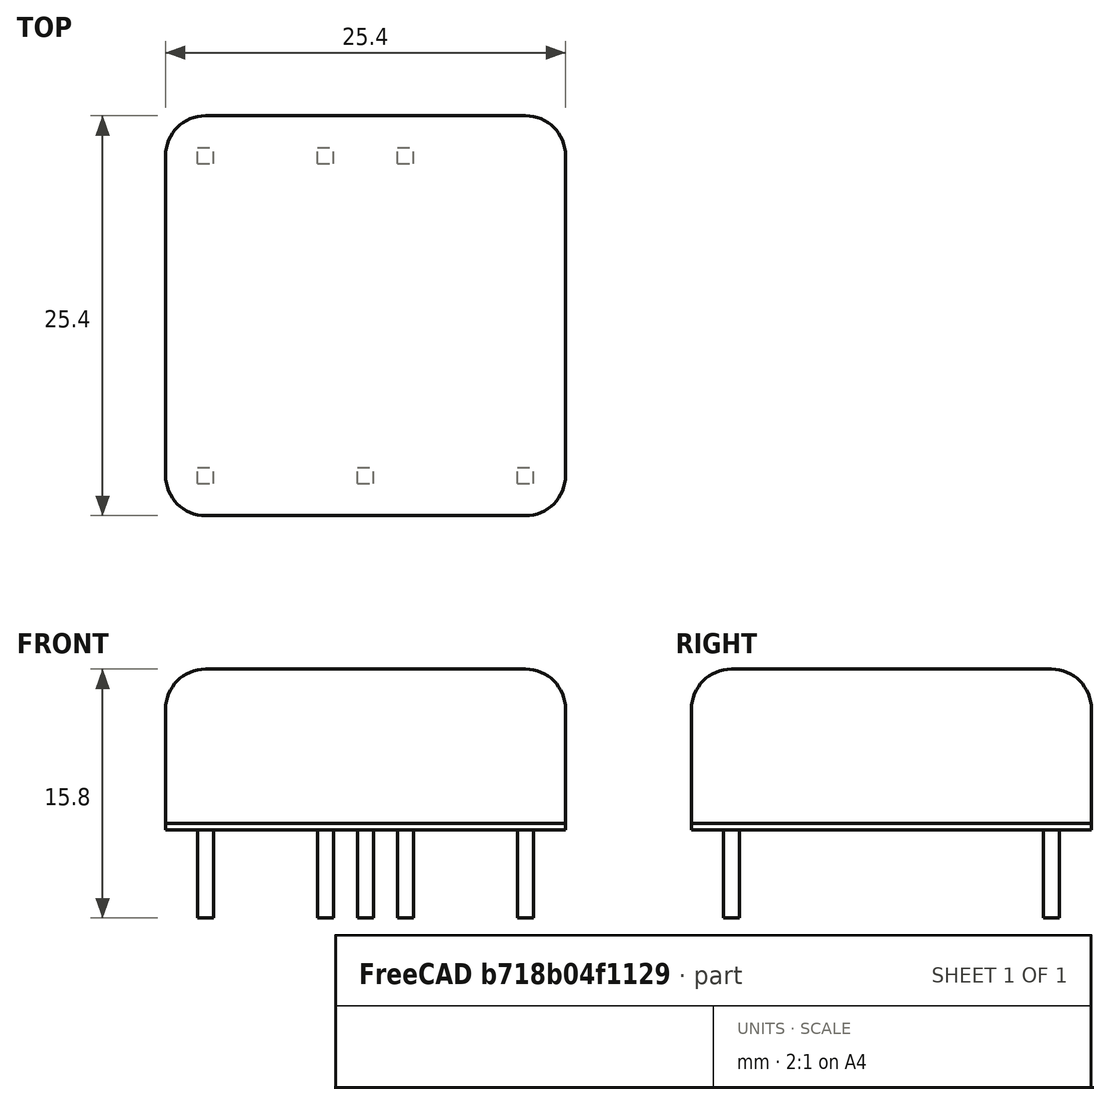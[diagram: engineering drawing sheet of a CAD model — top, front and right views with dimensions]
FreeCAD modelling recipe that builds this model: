
FCSTD DOCUMENT  (FreeCAD 0.18R4 (GitTag))
Label: PDQ15
License: All rights reserved
LicenseURL: http://en.wikipedia.org/wiki/All_rights_reserved
objects: Part::Box×8, Part::Fillet×3, Part::MultiFuse×1, Part::Part2DObjectPython×1
note: 13 computed .brp shape members not serialized (recipe doc carries the construction recipe); baked Part::Feature solids carry a one-line shape summary decoded from their .brp

FEATURE [Part::Box] Box  label="Cube"
  AttacherType = Attacher::AttachEngine3D
  Height = 0.4
  Length = 25.4
  Width = 25.4
FEATURE [Part::Fillet] Fillet  label="BottomPlastic"
  Base = -> Box
  Edges = 4 edges r=2.54: [Edge1,Edge3,Edge5,Edge7]
FEATURE [Part::Box] Box001  label="Pin3"
  AttacherType = Attacher::AttachEngine3D
  Height = 5.6
  Length = 1
  Placement = pos=(2.04,2.04,-5.6) rot=(0,0,1;0rad)
  Width = 1
FEATURE [Part::Box] Box002  label="Pin4"
  AttacherType = Attacher::AttachEngine3D
  Height = 5.6
  Length = 1
  Placement = pos=(12.2,2.04,-5.6) rot=(0,0,1;0rad)
  Width = 1
FEATURE [Part::Box] Box003  label="Pin5"
  AttacherType = Attacher::AttachEngine3D
  Height = 5.6
  Length = 1
  Placement = pos=(22.36,2.04,-5.6) rot=(0,0,1;0rad)
  Width = 1
FEATURE [Part::Box] Box004  label="Pin6"
  AttacherType = Attacher::AttachEngine3D
  Height = 5.6
  Length = 1
  Placement = pos=(2.04,22.36,-5.6) rot=(0,0,1;0rad)
  Width = 1
FEATURE [Part::Box] Box005  label="Pin2"
  AttacherType = Attacher::AttachEngine3D
  Height = 5.6
  Length = 1
  Placement = pos=(9.66,22.36,-5.6) rot=(0,0,1;0rad)
  Width = 1
FEATURE [Part::Box] Box006  label="Pin1"
  AttacherType = Attacher::AttachEngine3D
  Height = 5.6
  Length = 1
  Placement = pos=(14.74,22.36,-5.6) rot=(0,0,1;0rad)
  Width = 1
FEATURE [Part::MultiFuse] Fusion  label="Pins"
  Shapes = -> [Box001,Box002,Box006,Box005,Box004,Box003]
FEATURE [Part::Box] Box007  label="Cube001"
  AttacherType = Attacher::AttachEngine3D
  Height = 10.2
  Length = 25.4
  Width = 25.4
FEATURE [Part::Fillet] Fillet002  label="Fillet003"
  Base = -> Box007
  Edges = 4 edges r=2.54: [Edge1,Edge3,Edge5,Edge7]
FEATURE [Part::Fillet] Fillet003  label="TopPlastic"
  Base = -> Fillet002
  Edges = 8 edges r=2.54: [Edge1,Edge5,Edge6,Edge7,Edge8,Edge9,Edge10,Edge11]
FEATURE [Part::Part2DObjectPython] Rectangle  # Draft 2D object (typed FeaturePython)
  ChamferSize = 0
  Columns = 1
  FilletRadius = 0
  Height = 20.32
  Length = 20.32
  MakeFace = false
  Placement = pos=(2.54,2.54,10) rot=(0,0,1;0rad)
  Rows = 1
